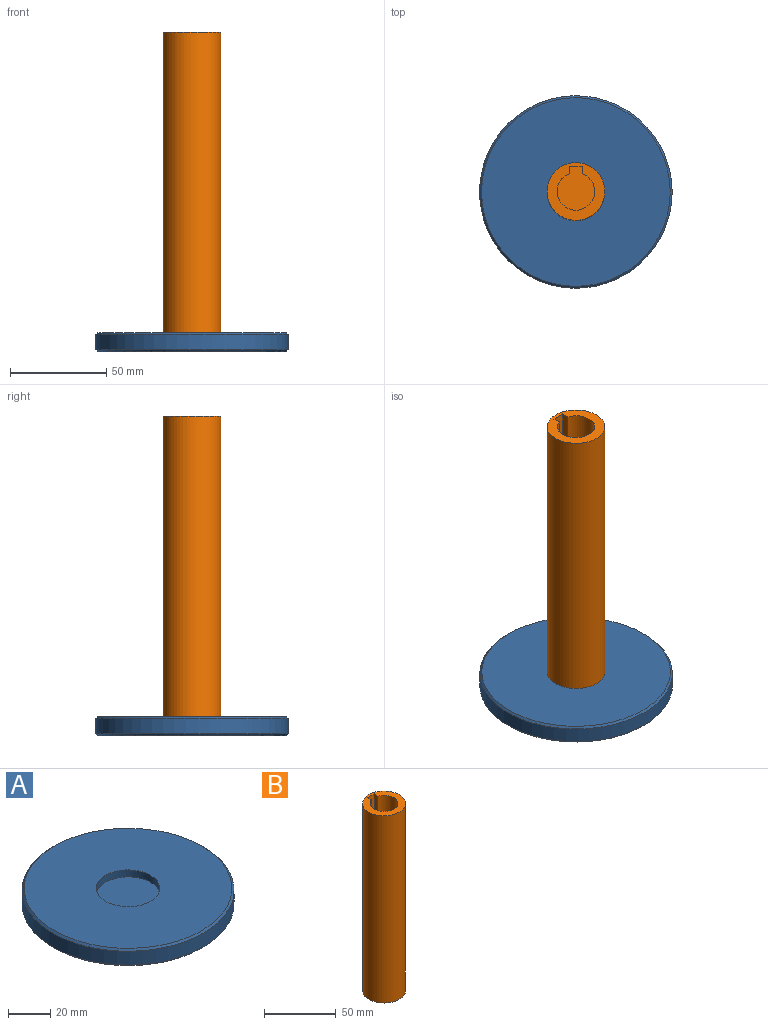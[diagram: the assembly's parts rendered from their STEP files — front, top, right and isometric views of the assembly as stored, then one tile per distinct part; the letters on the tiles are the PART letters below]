
ASSEMBLY  parts=2 mates=2
PART A: 7 faces, bbox 100x100x10 mm
  f0: cylinder r=50mm len=100mm, axis (0,0,-1), area 2513.3mm2, adj f5,f6
  f1: plane 98x98mm, normal (0,0,1), area 6836.1mm2, adj f3,f6
  f2: plane 98x98mm, normal (0,0,-1), area 7543mm2, adj f5
  f3: cylinder r=15mm len=30mm, axis (0,0,1), area 377mm2, adj f1,f4
  f4: plane 30x30mm, normal (0,0,1), area 706.9mm2, adj f3
  f5: cone r=50mm half-angle=45deg, axis (0,0,1), area 439.8mm2, adj f0,f2
  f6: cone r=49mm half-angle=45deg, axis (0,0,-1), area 439.8mm2, adj f0,f1
PART B: 8 faces, bbox 30x30x160 mm
  f0: cylinder r=15mm len=160mm, axis (0,0,-1), area 15079.6mm2, adj f1,f2
  f1: plane 30x30mm, normal (0,0,1), area 386.2mm2, adj f0,f3,f4,f5,f6
  f2: plane 30x30mm, normal (0,0,-1), area 706.9mm2, adj f0
  f3: plane 40x3.76mm, normal (1,0,0), area 150.3mm2, adj f1,f4,f6,f7
  f4: cylinder r=9.75mm len=40mm, axis (0,0,1), area 2185.4mm2, adj f1,f3,f5,f7
  f5: plane 40x3.76mm, normal (-1,0,0), area 150.3mm2, adj f1,f4,f6,f7
  f6: plane 40x6.5mm, normal (0,-1,0), area 260mm2, adj f1,f3,f5,f7
  f7: plane 22.7x19.5mm, normal (0,0,1), area 320.6mm2, adj f3,f4,f5,f6
PLACE A at identity
PLACE B t=(0,0,6)mm
MATE planar B.f0 <-> A.f3  axis (0,0,-1) through (0,0,6)mm
MATE cylindrical B.f0 <-> A.f3  axis (0,0,-1) through (0,0,6)mm
